# Revit family: 4433_Manual Call Point
name_source: partatom
category: Fire Alarm Devices
units: mm (PartAtom-declared; Revit-internal decimal feet)

## family parameters
Cut with Voids When Loaded = No
Host = Face
Maintain Annotation Orientation = No
OmniClass Number = 23.85.30.21
OmniClass Title = Environmental Detection/Registration
Part Type = Normal
Room Calculation Point = No
Round Connector Dimension = Use Diameter
Shared = No

## types (1)
- 4433
    Ambient Humidity = Maximum 90 % RH
    Ambient Temperature Operating = -10 to +55 °C
    Ambient Temperature Storage = -40 to +85 °C
    CPR = 0786-CPD-21235
    Current (Active) = 2.7mA
    Current Quiescent = 1.6mA
    Default Elevation = 0 mm  [stored 0 ft]
    Depth (mm) = 60 mm  [stored 0.19685 ft]
    Description = Addressable manual call point with isolator 4433
    Height (mm) = 87 mm  [stored 0.285433 ft]
    Ingress Protection Rating = IP42
    Manufacturer = Panasonic
    Max_Wire Size = Ø 1.6 mm (2 mm²)
    Min_Wire Size = Ø 0.8 mm (0.5 mm²)
    Model = 4433
    Omniclass Code = 23.85.30.21.11.11.11
    Omniclass Description = Smoke Detectors
    Product Material = FR ABS and polycarbonate_Panasonic_Red
    Short Circuit Isolator = Yes (Built-in)
    Tested and Approved = EN54-11, EN54-17
    Type Comments = The addressable manual call point 4433 with isolator is used for immediate manual actuation of a fire alarm. The 4433 has a configurable polling LED on the front and a polycarbonate flap to protect against accidental operation. For flush mounting or surface mounting
    URL = https://www.panasonic-fire-security.com
    Uniclass 2015 Code = Pr_75_80_30_27
    Uniclass 2015 Description = Fire and smoke detector bases
    Uniformat 2010  Code = D7050
    Uniformat 2010 Description = Detection and Alarm
    Vds Approval = G213004
    Version = RVT20
    Voltage Allowed = 12 – 30 VDC
    Voltage Normal = 24 VDC
    Weight = 201g
    Width (mm) = 87 mm  [stored 0.285433 ft]

note: [stored X ft] marks values corroborated as IEEE doubles in the binary element streams (Revit-internal decimal feet)

## geometry (parser evidence)
native form markers: Blend x71, Sweep x2
no freeform markers — native parametric forms only
